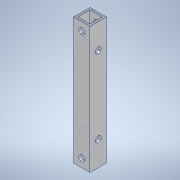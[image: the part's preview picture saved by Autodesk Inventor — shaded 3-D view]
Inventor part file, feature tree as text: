
AUTODESK INVENTOR PART (.ipt)
format: ipt  version: 2020.3 (Build 243373000, 373)  size: 144,896 bytes
history: native  units: mm
features: sketch x4, hole x3, other x1, extrude x1
ambient origin geometry x8: Origin, YZ Plane, XZ Plane, XY Plane, X Axis, Y Axis, Z Axis, Center Point
bodies: Body1 (feature_tree)
feature tree (9):
  other  "ソリッド1"
  extrude  "押し出し1"  Depth=9.0mm
  hole  "穴1"  [1 undecoded]
  hole  "穴2"  [1 undecoded]
  hole  "穴3"  [1 undecoded]
  sketch  "スケッチ1"
  sketch  "スケッチ2"
  sketch  "スケッチ3"
  sketch  "スケッチ4"
note: 3 required parameter values undecoded (feature->parameter linkage not recoverable at this tier; creation-order binding heuristic only, values carry confidence <= 0.55)
